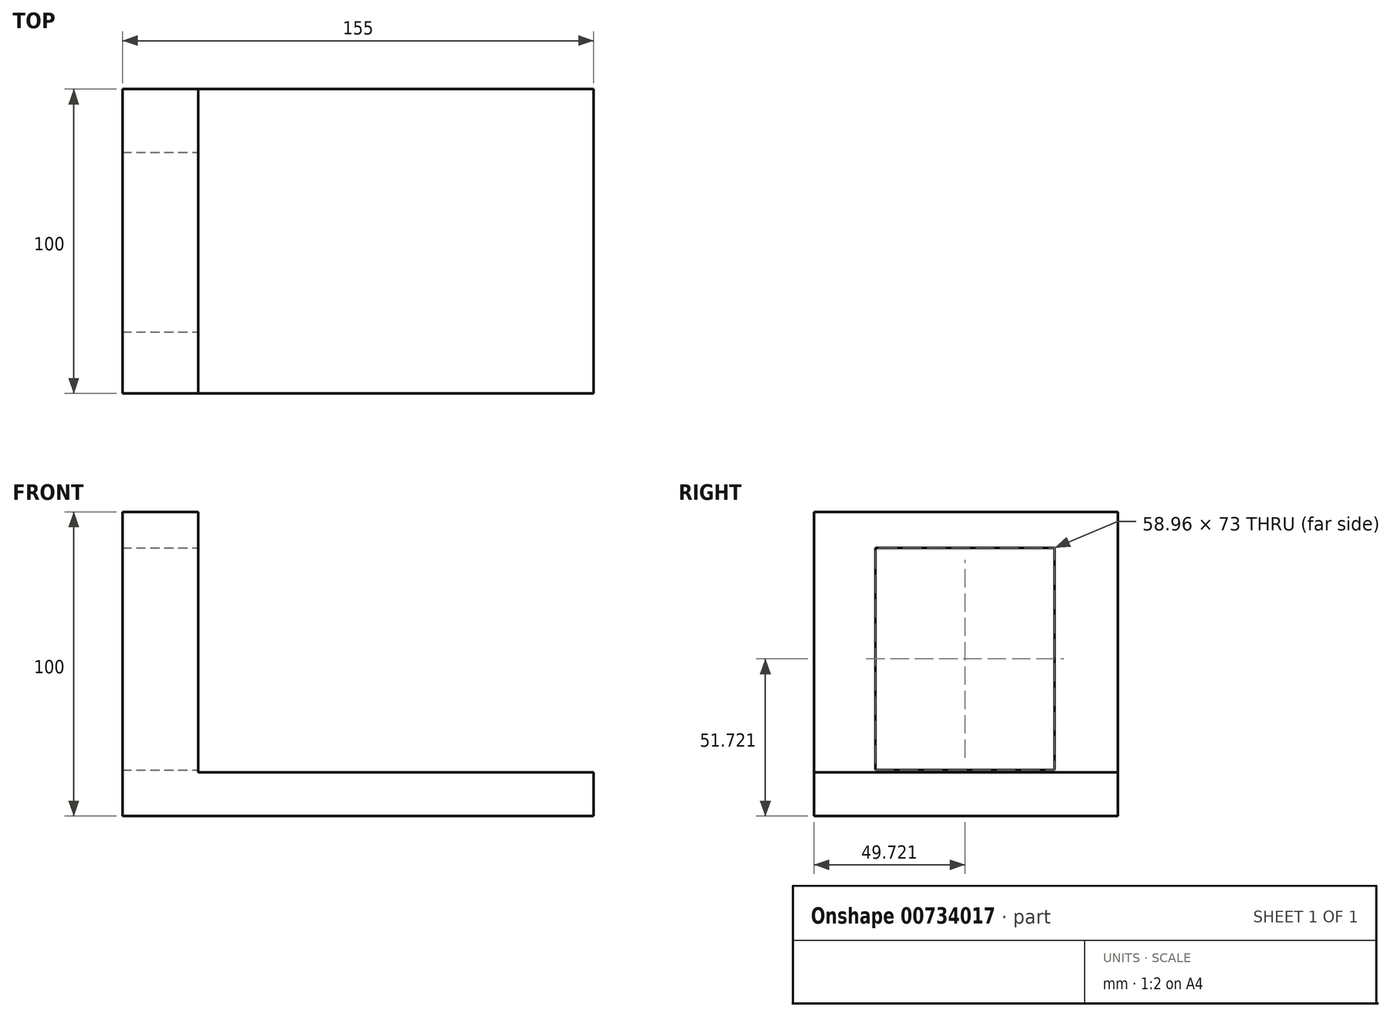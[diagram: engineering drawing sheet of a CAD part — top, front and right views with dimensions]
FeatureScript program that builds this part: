
annotation { "Feature Type Name" : "Feature", "Feature Type Description" : "" }
export const myFeature = defineFeature(function(context is Context, id is Id, definition is map)
    precondition{}
    {
        {
            var Q0;
            Q0=qCreatedBy(makeId("Right.planeOp"),FACE);
            var sketch = newSketch(context, id + "F0", { "sketchPlane" : qUnion([Q0])});
            skLineSegment(sketch, "E0.bottom", {"start": v(-45.1, 75.37) * mm, "end": v(54.9, 75.37) * mm});
            skLineSegment(sketch, "E0.top", {"start": v(-45.1, -24.63) * mm, "end": v(54.9, -24.63) * mm});
            skLineSegment(sketch, "E0.left", {"start": v(-45.1, 75.37) * mm, "end": v(-45.1, -24.63) * mm});
            skLineSegment(sketch, "E0.right", {"start": v(54.9, 75.37) * mm, "end": v(54.9, -24.63) * mm});
            skSolve(sketch);
        }
        {
            var Q0;
            Q0=makeQuery(id+"F0.imprint","IMPRINT",FACE,{"disambiguationData":[TD([[makeQuery(id+"F0.imprint","IMPRINT",EDGE,{"derivedFrom":sQuery(id+"F0.wireOp",EDGE,"E0.bottom")}),-1.0]])]});
            extrude(context, id + "F1", {"entities" : qUnion([Q0]), "depth" : 25 * mm, "offsetDistance" : 25 * mm});
        }
        {
            var Q0;
            Q0=makeQuery(id+"F1.opExtrude","CAP_FACE",FACE,{"disambiguationData":[OSD([sQuery(id+"F0.wireOp",EDGE,"E0.bottom"),sQuery(id+"F0.wireOp",EDGE,"E0.top"),sQuery(id+"F0.wireOp",EDGE,"E0.left"),sQuery(id+"F0.wireOp",EDGE,"E0.right")])],"isStart":false});
            var sketch = newSketch(context, id + "F2", { "sketchPlane" : qUnion([Q0])});
            skLineSegment(sketch, "E1.bottom", {"start": v(-24.87, 63.6) * mm, "end": v(34.1, 63.6) * mm});
            skLineSegment(sketch, "E1.top", {"start": v(-24.87, -9.4) * mm, "end": v(34.1, -9.4) * mm});
            skLineSegment(sketch, "E1.left", {"start": v(-24.87, 63.6) * mm, "end": v(-24.87, -9.4) * mm});
            skLineSegment(sketch, "E1.right", {"start": v(34.1, 63.6) * mm, "end": v(34.1, -9.4) * mm});
            skSolve(sketch);
        }
        {
            var Q0;
            Q0 = qSketchRegion(id + "F2", true);
            extrude(context, id + "F3", {"entities" : qUnion([Q0]), "operationType" : NewBodyOperationType.REMOVE, "oppositeDirection" : true, "depth" : 25 * mm, "offsetDistance" : 25 * mm});
        }
        {
            var Q0;
            Q0=makeQuery(id+"F1.opExtrude","CAP_FACE",FACE,{"disambiguationData":[OSD([sQuery(id+"F0.wireOp",EDGE,"E0.bottom"),sQuery(id+"F0.wireOp",EDGE,"E0.top"),sQuery(id+"F0.wireOp",EDGE,"E0.left"),sQuery(id+"F0.wireOp",EDGE,"E0.right")])],"isStart":false});
            var sketch = newSketch(context, id + "F4", { "sketchPlane" : qUnion([Q0])});
            skLineSegment(sketch, "E2.bottom", {"start": v(-45.1, -10.18) * mm, "end": v(54.9, -10.18) * mm});
            skLineSegment(sketch, "E2.top", {"start": v(-45.1, -24.63) * mm, "end": v(54.9, -24.63) * mm});
            skLineSegment(sketch, "E2.left", {"start": v(-45.1, -10.18) * mm, "end": v(-45.1, -24.63) * mm});
            skLineSegment(sketch, "E2.right", {"start": v(54.9, -10.18) * mm, "end": v(54.9, -24.63) * mm});
            skSolve(sketch);
        }
        {
            var Q0;
            Q0=makeQuery(id+"F4.imprint","IMPRINT",FACE,{"disambiguationData":[TD([[makeQuery(id+"F4.imprint","IMPRINT",EDGE,{"derivedFrom":sQuery(id+"F4.wireOp",EDGE,"E2.bottom")}),-1.0]])]});
            extrude(context, id + "F5", {"entities" : qUnion([Q0]), "operationType" : NewBodyOperationType.ADD, "depth" : 130 * mm, "offsetDistance" : 25 * mm});
        }
    });
